# Revit family: PIA-101_RFA
name_source: partatom
category: Aparatos sanitarios
units: mm (PartAtom-declared; Revit-internal decimal feet)

## family parameters
Activar corte en vistas = No
Compartido = Sí
Corte con vacíos al cargar = No
Cota de conector redondo = Usar diámetro
Mantener orientación de anotación = No
Número OmniClass = 23.45.55.14
Punto de cálculo de habitación = Sí
Se basa en plano de trabajo = No
Siempre vertical = Sí
Tipo de pieza = Normal
Título OmniClass = Single Faucets

## types (1)
- PIA-101
    Chrome = Brass Chromed
    Comentarios de tipo = Monomando alto para lavabo.
    Conexión AF = Sí
    Connection = ½" - 14 NPSM
    Descripción = Monomando alto de lavabo sin contra.
    Elevación por defecto = 35 "
    Fabricante = Helvex
    Imagen de tipo = PIA-101.jpg
    Instructive = https://helvex.com.mx
    Max. Working Pressure = 85.3 psi
    Min. Working Pressure = 7.1 psi
    Modelo = PIA-101
    Total Depth = 7 "
    Total Height = 11 "
    Total Width = 2 "
    URL = https://helvex.com.mx

## geometry (parser evidence)
native form markers: Sweep x3
no freeform markers — native parametric forms only
